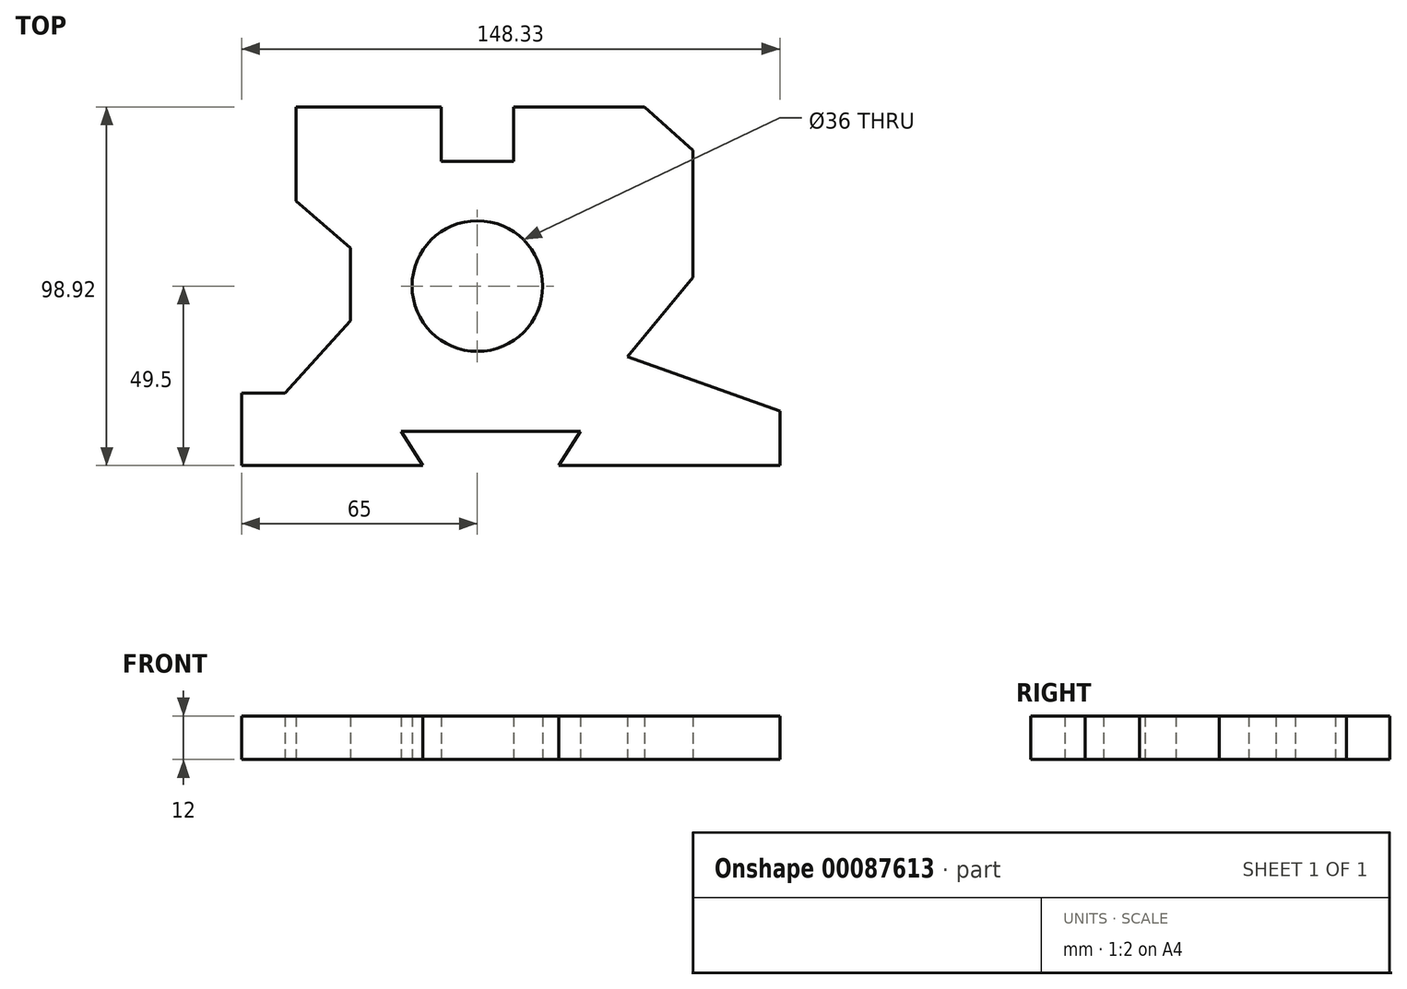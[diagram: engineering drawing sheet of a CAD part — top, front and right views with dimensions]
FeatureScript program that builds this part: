
annotation { "Feature Type Name" : "Feature", "Feature Type Description" : "" }
export const myFeature = defineFeature(function(context is Context, id is Id, definition is map)
    precondition{}
    {
        {
            var Q0;
            Q0=qCreatedBy(makeId("Top.planeOp"),FACE);
            var sketch = newSketch(context, id + "F0", { "sketchPlane" : qUnion([Q0])});
            skLineSegment(sketch, "E0", {"start": v(0, 0) * mm, "end": v(50, 0) * mm});
            skLineSegment(sketch, "E1", {"start": v(50, 0) * mm, "end": v(44, 9.42) * mm});
            skLineSegment(sketch, "E2", {"start": v(44, 9.42) * mm, "end": v(93.4, 9.42) * mm});
            skLineSegment(sketch, "E3", {"start": v(93.4, 9.42) * mm, "end": v(87.4, 0) * mm});
            skLineSegment(sketch, "E4", {"start": v(87.4, 0) * mm, "end": v(148.33, 0) * mm});
            skLineSegment(sketch, "E5", {"start": v(148.33, 0) * mm, "end": v(148.33, 15) * mm});
            skLineSegment(sketch, "E6", {"start": v(148.33, 15) * mm, "end": v(106.33, 30) * mm});
            skLineSegment(sketch, "E7", {"start": v(106.33, 30) * mm, "end": v(124.33, 51.92) * mm});
            skLineSegment(sketch, "E8", {"start": v(124.33, 51.92) * mm, "end": v(124.33, 86.92) * mm});
            skLineSegment(sketch, "E9", {"start": v(124.33, 86.92) * mm, "end": v(111, 98.92) * mm});
            skLineSegment(sketch, "E10", {"start": v(111, 98.92) * mm, "end": v(75, 98.92) * mm});
            skLineSegment(sketch, "E11", {"start": v(75, 98.92) * mm, "end": v(75, 83.92) * mm});
            skLineSegment(sketch, "E12", {"start": v(75, 83.92) * mm, "end": v(55, 83.92) * mm});
            skLineSegment(sketch, "E13", {"start": v(55, 83.92) * mm, "end": v(55, 98.92) * mm});
            skLineSegment(sketch, "E14", {"start": v(55, 98.92) * mm, "end": v(15, 98.92) * mm});
            skLineSegment(sketch, "E15", {"start": v(15, 98.92) * mm, "end": v(15, 72.92) * mm});
            skLineSegment(sketch, "E16", {"start": v(15, 72.92) * mm, "end": v(30, 60) * mm});
            skLineSegment(sketch, "E17", {"start": v(30, 60) * mm, "end": v(30, 40) * mm});
            skLineSegment(sketch, "E18", {"start": v(30, 40) * mm, "end": v(12, 20) * mm});
            skLineSegment(sketch, "E19", {"start": v(12, 20) * mm, "end": v(0, 20) * mm});
            skLineSegment(sketch, "E20", {"start": v(0, 20) * mm, "end": v(0, 0) * mm});
            skCircle(sketch, "E21", {"center": v(65, 49.5) * mm, "radius": 18 * mm});
            skSolve(sketch);
        }
        {
            var Q0;
            Q0 = qSketchRegion(id + "F0", true);
            extrude(context, id + "F1", {"entities" : qUnion([Q0]), "depth" : 12 * mm});
        }
    });
